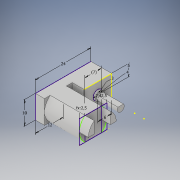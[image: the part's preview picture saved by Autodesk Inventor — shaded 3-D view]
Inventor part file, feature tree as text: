
AUTODESK INVENTOR PART (.ipt)
format: ipt  version: 2019 (Build 230136000, 136)  size: 174,592 bytes
history: native  units: mm
features: extrude x10, sketch x6, other x1
ambient origin geometry x8: Origin, YZ Plane, XZ Plane, XY Plane, X Axis, Y Axis, Z Axis, Center Point
bodies: Solid1 (feature_tree)
feature tree (17):
  sketch  "Sketch1"  dims[d0=24.0mm d1=10.0mm]
  extrude  "Extrusion1"  Depth=10.0mm
  extrude  "Extrusion2"  Depth=19.0mm TaperAngle=0.0deg
  sketch  "Sketch2"  dims[d2=12.0mm d3=19.0mm d4=0.0mm]
  extrude  "Extrusion3"  Depth=4.0mm
  extrude  "Extrusion4"  Depth=6.0mm
  extrude  "Extrusion5"  Depth=2.4mm
  sketch  "Sketch3"  dims[d5=9.0mm d6=0.0mm d7=4.0mm]
  extrude  "Extrusion6"  Depth=10.0mm TaperAngle=0.0deg
  extrude  "Extrusion7"  Depth=1.0mm TaperAngle=0.0deg
  extrude  "Extrusion8"  Depth=2.5mm
  extrude  "Extrusion9"  Depth=2.5mm
  other  "Work Axis1"
  sketch  "Sketch5"  dims[d10=3.0mm d11=2.4mm]
  extrude  "Extrusion10"  Depth=4.0mm
  sketch  "Sketch4"  dims[d8=5.0mm d9=6.0mm]
  sketch  "Sketch6"  dims[d12=1.0mm d13=0.0mm d14=10.0mm d15=0.0mm d16=1.0mm d17=0.0mm d18=2.5mm d19=2.5mm d20=7.0mm d21=15.0mm d22=0.0mm d23=15.0mm d24=0.0mm d25=4.0mm d26=0.0mm d27=4.0mm d28=0.0mm d29=8.0mm d30=0.0mm]
